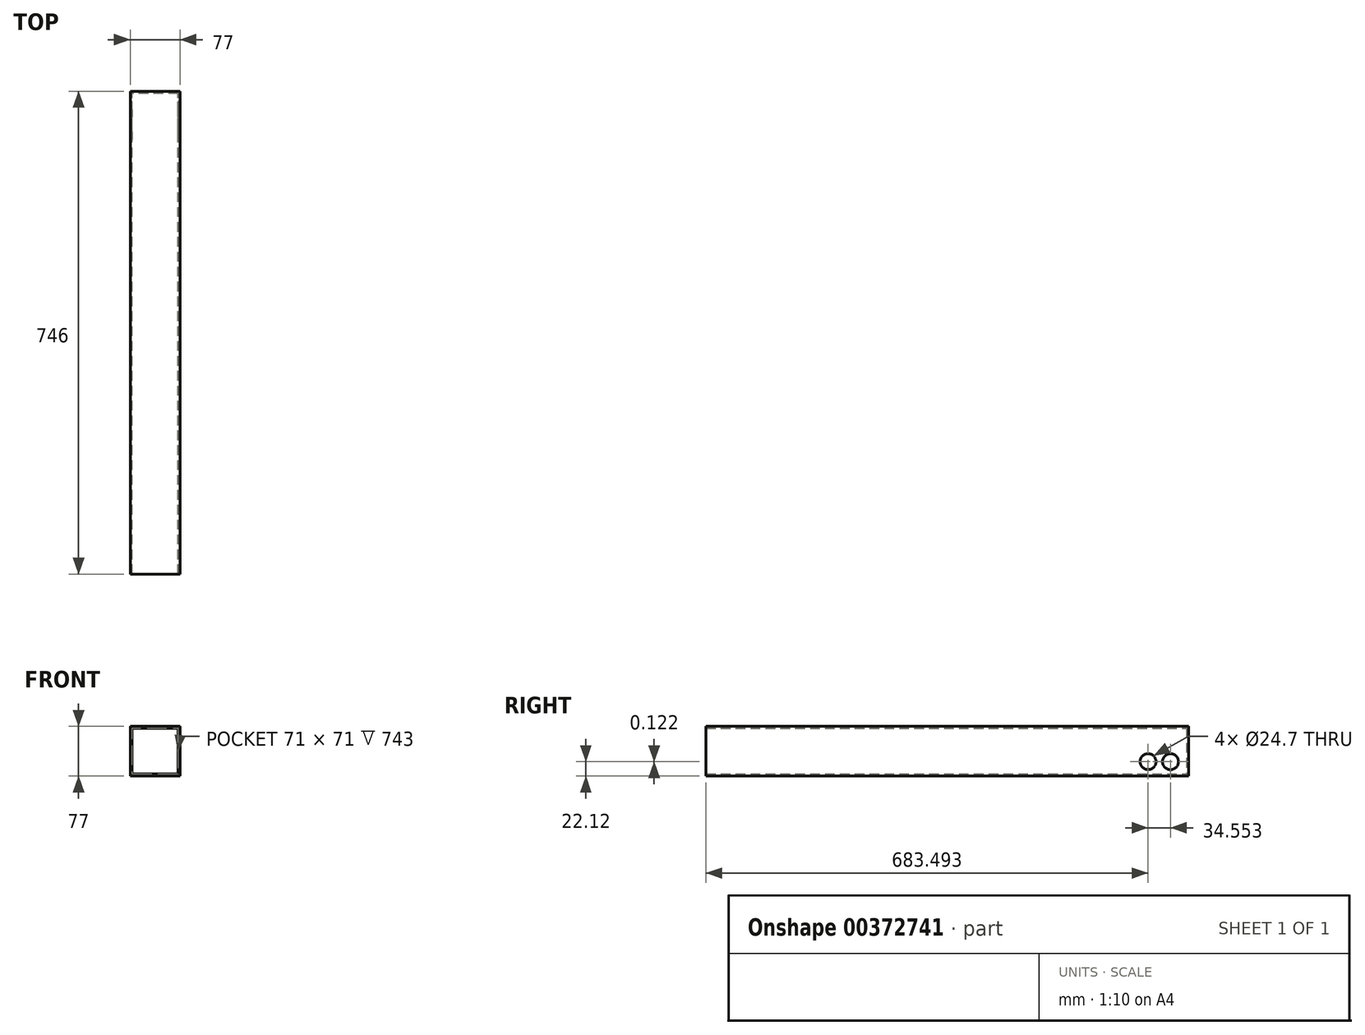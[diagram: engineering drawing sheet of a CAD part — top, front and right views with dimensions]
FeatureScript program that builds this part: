
annotation { "Feature Type Name" : "Feature", "Feature Type Description" : "" }
export const myFeature = defineFeature(function(context is Context, id is Id, definition is map)
    precondition{}
    {
        {
            var Q0;
            Q0=qCreatedBy(makeId("Front.planeOp"),FACE);
            var sketch = newSketch(context, id + "F0", { "sketchPlane" : qUnion([Q0])});
            skLineSegment(sketch, "E0.bottom", {"start": v(38.5, 38.5) * mm, "end": v(-38.5, 38.5) * mm});
            skLineSegment(sketch, "E0.top", {"start": v(38.5, -38.5) * mm, "end": v(-38.5, -38.5) * mm});
            skLineSegment(sketch, "E0.left", {"start": v(38.5, 38.5) * mm, "end": v(38.5, -38.5) * mm});
            skLineSegment(sketch, "E0.right", {"start": v(-38.5, 38.5) * mm, "end": v(-38.5, -38.5) * mm});
            skPoint(sketch, "E0.middle", {"position": v(0, 0) * mm});
            skSolve(sketch);
        }
        {
            var Q0;
            Q0 = qSketchRegion(id + "F0", true);
            extrude(context, id + "F1", {"entities" : qUnion([Q0]), "depth" : 746 * mm});
        }
        {
            var Q0;
            Q0=makeQuery(id+"F1.opExtrude","CAP_FACE",FACE,{"disambiguationData":[OSD([sQuery(id+"F0.wireOp",EDGE,"E0.bottom"),sQuery(id+"F0.wireOp",EDGE,"E0.top"),sQuery(id+"F0.wireOp",EDGE,"E0.left"),sQuery(id+"F0.wireOp",EDGE,"E0.right")])],"isStart":false});
            shell(context, id + "F2", {"entities" : qUnion([Q0]), "thickness" : 3 * mm});
        }
        {
            var Q0;
            Q0=makeQuery(id+"F1.opExtrude","SWEPT_FACE",FACE,{"disambiguationData":[OSD([sQuery(id+"F0.wireOp",EDGE,"E0.right")])]});
            var sketch = newSketch(context, id + "F3", { "sketchPlane" : qUnion([Q0])});
            skCircle(sketch, "E1", {"center": v(27.95, -16.38) * mm, "radius": 12.35 * mm});
            skSolve(sketch);
        }
        {
            var Q0;
            Q0=sQuery(id+"F3.wireOp",VERTEX,"E1.center");
            var Q1;
            Q1=makeQuery(id+"F1.opExtrude","SWEPT_BODY",BODY,{"disambiguationData":[OSD([sQuery(id+"F0.wireOp",EDGE,"E0.bottom"),sQuery(id+"F0.wireOp",EDGE,"E0.top"),sQuery(id+"F0.wireOp",EDGE,"E0.left"),sQuery(id+"F0.wireOp",EDGE,"E0.right")])]});
            hole(context, id + "F4", {"style" : HoleStyle.SIMPLE, "endStyle" : HoleEndStyle.THROUGH, "holeDiameter" : 24.7 * mm, "isTappedThrough" : true, "tappedDepth" : 12 * mm, "tapClearance" : 3, "locations" : qUnion([Q0]), "scope" : qUnion([Q1])});
        }
        {
            var Q0;
            Q0=makeQuery(id+"F1.opExtrude","SWEPT_FACE",FACE,{"disambiguationData":[OSD([sQuery(id+"F0.wireOp",EDGE,"E0.right")])]});
            var sketch = newSketch(context, id + "F5", { "sketchPlane" : qUnion([Q0])});
            skCircle(sketch, "E2", {"center": v(62.5, -16.26) * mm, "radius": 12.35 * mm});
            skSolve(sketch);
        }
        {
            var Q0;
            Q0=sQuery(id+"F5.wireOp",VERTEX,"E2.center");
            var Q1;
            Q1=makeQuery(id+"F1.opExtrude","SWEPT_BODY",BODY,{"disambiguationData":[OSD([sQuery(id+"F0.wireOp",EDGE,"E0.bottom"),sQuery(id+"F0.wireOp",EDGE,"E0.top"),sQuery(id+"F0.wireOp",EDGE,"E0.left"),sQuery(id+"F0.wireOp",EDGE,"E0.right")])]});
            hole(context, id + "F6", {"style" : HoleStyle.SIMPLE, "endStyle" : HoleEndStyle.THROUGH, "holeDiameter" : 24.7 * mm, "isTappedThrough" : true, "tappedDepth" : 12 * mm, "tapClearance" : 3, "locations" : qUnion([Q0]), "scope" : qUnion([Q1])});
        }
    });
